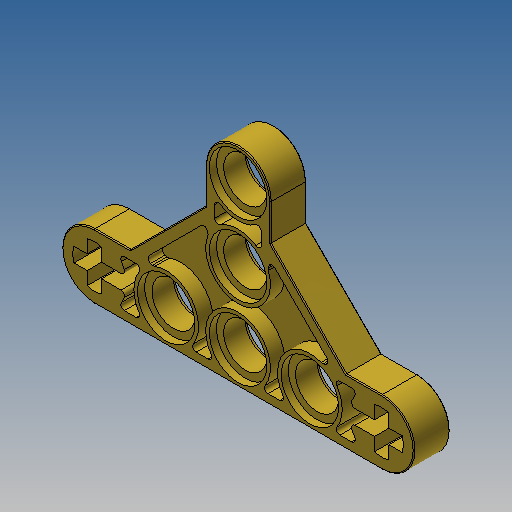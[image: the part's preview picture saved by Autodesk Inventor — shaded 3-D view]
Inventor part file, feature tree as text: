
AUTODESK INVENTOR PART (.ipt)
format: ipt  version: 2025 (Build 290162010, 162A)  size: 410,624 bytes
history: native  units: in
note: dims shown in document units (in); Inventor stores cm internally (conversion verified against a paired STEP export)
features: extrude x3, sketch x2, mirror x1, fillet x1
ambient origin geometry x8: Origin, YZ Plane, XZ Plane, XY Plane, X Axis, Y Axis, Z Axis, Center Point
bodies: Solid1 (feature_tree)
feature tree (7):
  sketch  "Sketch1"  dims[d0=0.315in d1=0.189in]
  extrude  "Extrusion1"  Depth=0.315in
  extrude  "Extrusion2"  Depth=0.2835in
  extrude  "Extrusion3"  Depth=0.0394in
  mirror  "Mirror1"
  fillet  "Fillet1"  Radius=0.0394in
  sketch  "Sketch2"  dims[d2=0.189in d3=0.2835in d5=0.0394in d6=0.0394in d7=0.063in d8=0.063in d9=0.1575in d10=0.0in d11=0.0315in d12=0.0in d13=0.252in d14=0.0315in d15=0.0in d16=0.0039in d17=0.1575in d18=0.0445in d20=15.0deg d21=0.0157in]
